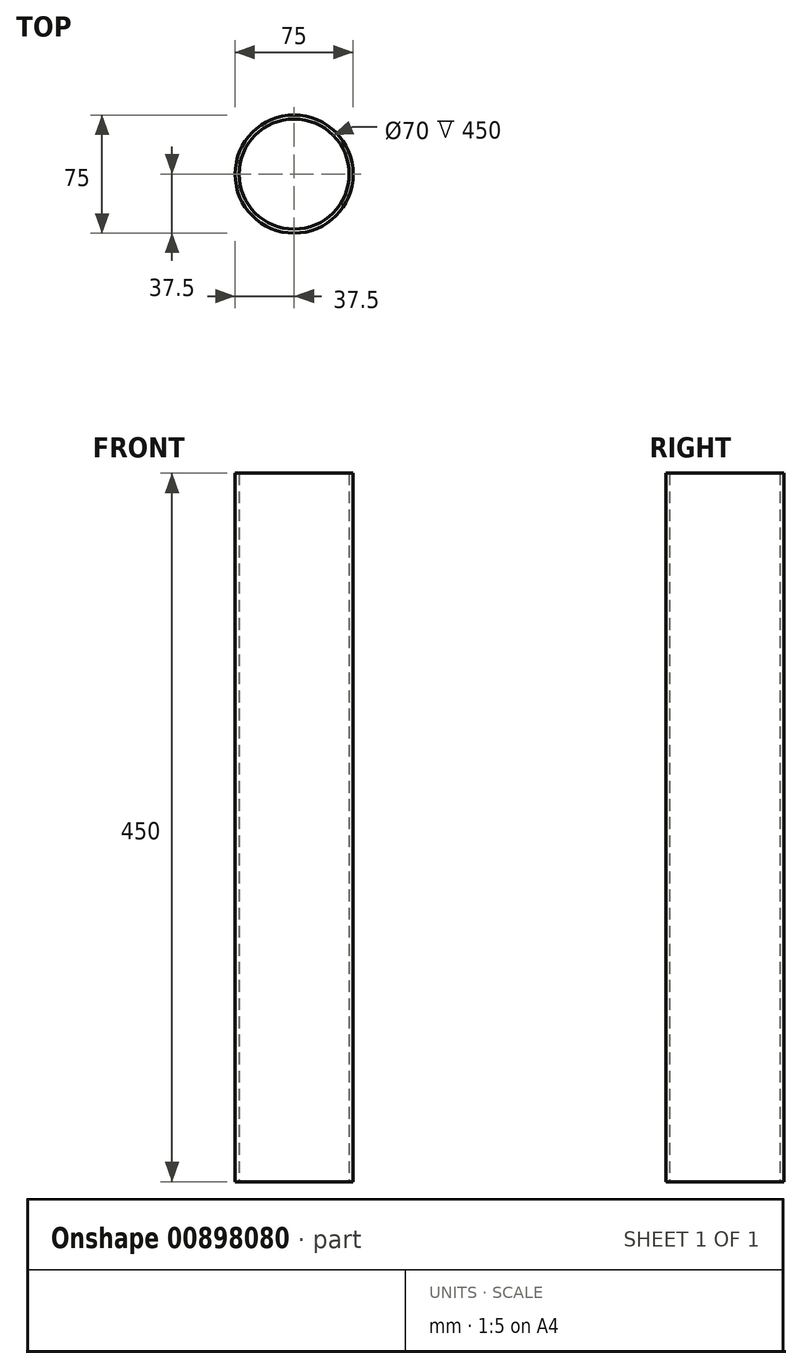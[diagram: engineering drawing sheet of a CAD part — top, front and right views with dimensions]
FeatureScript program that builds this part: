
annotation { "Feature Type Name" : "Feature", "Feature Type Description" : "" }
export const myFeature = defineFeature(function(context is Context, id is Id, definition is map)
    precondition{}
    {
        {
            var Q0;
            Q0=qCreatedBy(makeId("Top.planeOp"),FACE);
            var sketch = newSketch(context, id + "F0", { "sketchPlane" : qUnion([Q0])});
            skCircle(sketch, "E0", {"center": v(0, 0) * mm, "radius": 35 * mm});
            skCircle(sketch, "E1", {"center": v(0, 0) * mm, "radius": 37.5 * mm});
            skSolve(sketch);
        }
        {
            var Q0;
            Q0 = qSketchRegion(id + "F0", true);
            extrude(context, id + "F1", {"entities" : qUnion([Q0]), "depth" : 450 * mm, "offsetDistance" : 25 * mm});
        }
    });
